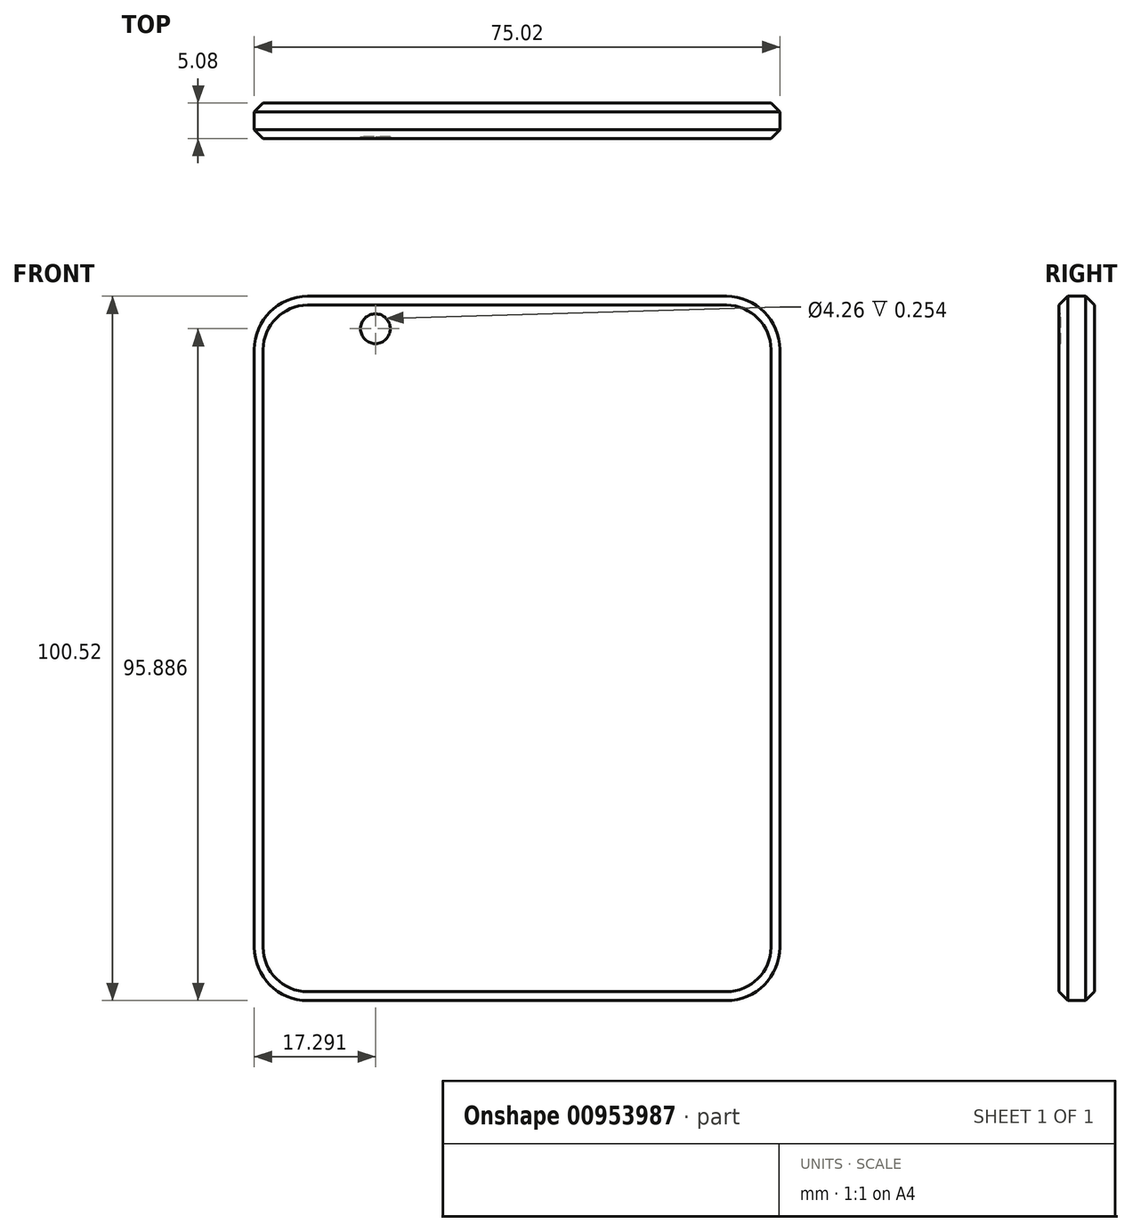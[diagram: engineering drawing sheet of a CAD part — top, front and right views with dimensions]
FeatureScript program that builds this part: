
annotation { "Feature Type Name" : "Feature", "Feature Type Description" : "" }
export const myFeature = defineFeature(function(context is Context, id is Id, definition is map)
    precondition{}
    {
        {
            var Q0;
            Q0=qCreatedBy(makeId("Front.planeOp"),FACE);
            var sketch = newSketch(context, id + "F0", { "sketchPlane" : qUnion([Q0])});
            skLineSegment(sketch, "E0.bottom", {"start": v(37.51, -50.26) * mm, "end": v(-37.51, -50.26) * mm});
            skLineSegment(sketch, "E0.top", {"start": v(37.51, 50.26) * mm, "end": v(-37.51, 50.26) * mm});
            skLineSegment(sketch, "E0.left", {"start": v(37.51, -50.26) * mm, "end": v(37.51, 50.26) * mm});
            skLineSegment(sketch, "E0.right", {"start": v(-37.51, -50.26) * mm, "end": v(-37.51, 50.26) * mm});
            skPoint(sketch, "E0.middle", {"position": v(0, 0) * mm});
            skSolve(sketch);
        }
        {
            var Q0;
            Q0=makeQuery(id+"F0.imprint","IMPRINT",FACE,{"disambiguationData":[TD([[makeQuery(id+"F0.imprint","IMPRINT",EDGE,{"derivedFrom":sQuery(id+"F0.wireOp",EDGE,"E0.bottom")}),-1.0]])]});
            extrude(context, id + "F1", {"entities" : qUnion([Q0]), "depth" : 5.08 * mm, "offsetDistance" : 25.4 * mm});
        }
        {
            var Q0;
            Q0=makeQuery(id+"F1.opExtrude","SWEPT_EDGE",EDGE,{"disambiguationData":[OSD([sQuery(id+"F0.wireOp",EDGE,"E0.top"),sQuery(id+"F0.wireOp",EDGE,"E0.right")])]});
            var Q1;
            Q1=makeQuery(id+"F1.opExtrude","SWEPT_EDGE",EDGE,{"disambiguationData":[OSD([sQuery(id+"F0.wireOp",EDGE,"E0.bottom"),sQuery(id+"F0.wireOp",EDGE,"E0.right")])]});
            var Q2;
            Q2=makeQuery(id+"F1.opExtrude","SWEPT_EDGE",EDGE,{"disambiguationData":[OSD([sQuery(id+"F0.wireOp",EDGE,"E0.top"),sQuery(id+"F0.wireOp",EDGE,"E0.left")])]});
            var Q3;
            Q3=makeQuery(id+"F1.opExtrude","SWEPT_EDGE",EDGE,{"disambiguationData":[OSD([sQuery(id+"F0.wireOp",EDGE,"E0.bottom"),sQuery(id+"F0.wireOp",EDGE,"E0.left")])]});
            fillet(context, id + "F2", {"entities" : qUnion([Q0, Q1, Q2, Q3]), "radius" : 7.62 * mm, "tangentPropagation" : true, "allowEdgeOverflow" : false});
        }
        {
            var Q0;
            Q0=makeQuery(id+"F1.opExtrude","CAP_FACE",FACE,{"disambiguationData":[OSD([sQuery(id+"F0.wireOp",EDGE,"E0.bottom"),sQuery(id+"F0.wireOp",EDGE,"E0.top"),sQuery(id+"F0.wireOp",EDGE,"E0.left"),sQuery(id+"F0.wireOp",EDGE,"E0.right")])],"isStart":false});
            chamfer(context, id + "F3", {"entities" : qUnion([Q0]), "width" : 1.27 * mm, "tangentPropagation" : true});
        }
        {
            var Q0;
            Q0=makeQuery(id+"F1.opExtrude","CAP_FACE",FACE,{"disambiguationData":[OSD([sQuery(id+"F0.wireOp",EDGE,"E0.bottom"),sQuery(id+"F0.wireOp",EDGE,"E0.top"),sQuery(id+"F0.wireOp",EDGE,"E0.left"),sQuery(id+"F0.wireOp",EDGE,"E0.right")])],"isStart":false});
            var sketch = newSketch(context, id + "F4", { "sketchPlane" : qUnion([Q0])});
            skCircle(sketch, "E1", {"center": v(-20.22, 45.63) * mm, "radius": 2.13 * mm});
            skSolve(sketch);
        }
        {
            var Q0;
            Q0=makeQuery(id+"F4.imprint","IMPRINT",FACE,{"disambiguationData":[TD([[makeQuery(id+"F4.imprint","IMPRINT",EDGE,{"derivedFrom":sQuery(id+"F4.wireOp",EDGE,"E1")}),1.0]])]});
            extrude(context, id + "F5", {"entities" : qUnion([Q0]), "operationType" : NewBodyOperationType.REMOVE, "oppositeDirection" : true, "depth" : 0.25 * mm, "offsetDistance" : 25.4 * mm});
        }
        {
            var Q0;
            Q0=makeQuery(id+"F1.opExtrude","CAP_FACE",FACE,{"disambiguationData":[OSD([sQuery(id+"F0.wireOp",EDGE,"E0.bottom"),sQuery(id+"F0.wireOp",EDGE,"E0.top"),sQuery(id+"F0.wireOp",EDGE,"E0.left"),sQuery(id+"F0.wireOp",EDGE,"E0.right")])],"isStart":true});
            chamfer(context, id + "F6", {"entities" : qUnion([Q0]), "width" : 1.27 * mm, "tangentPropagation" : true});
        }
    });
